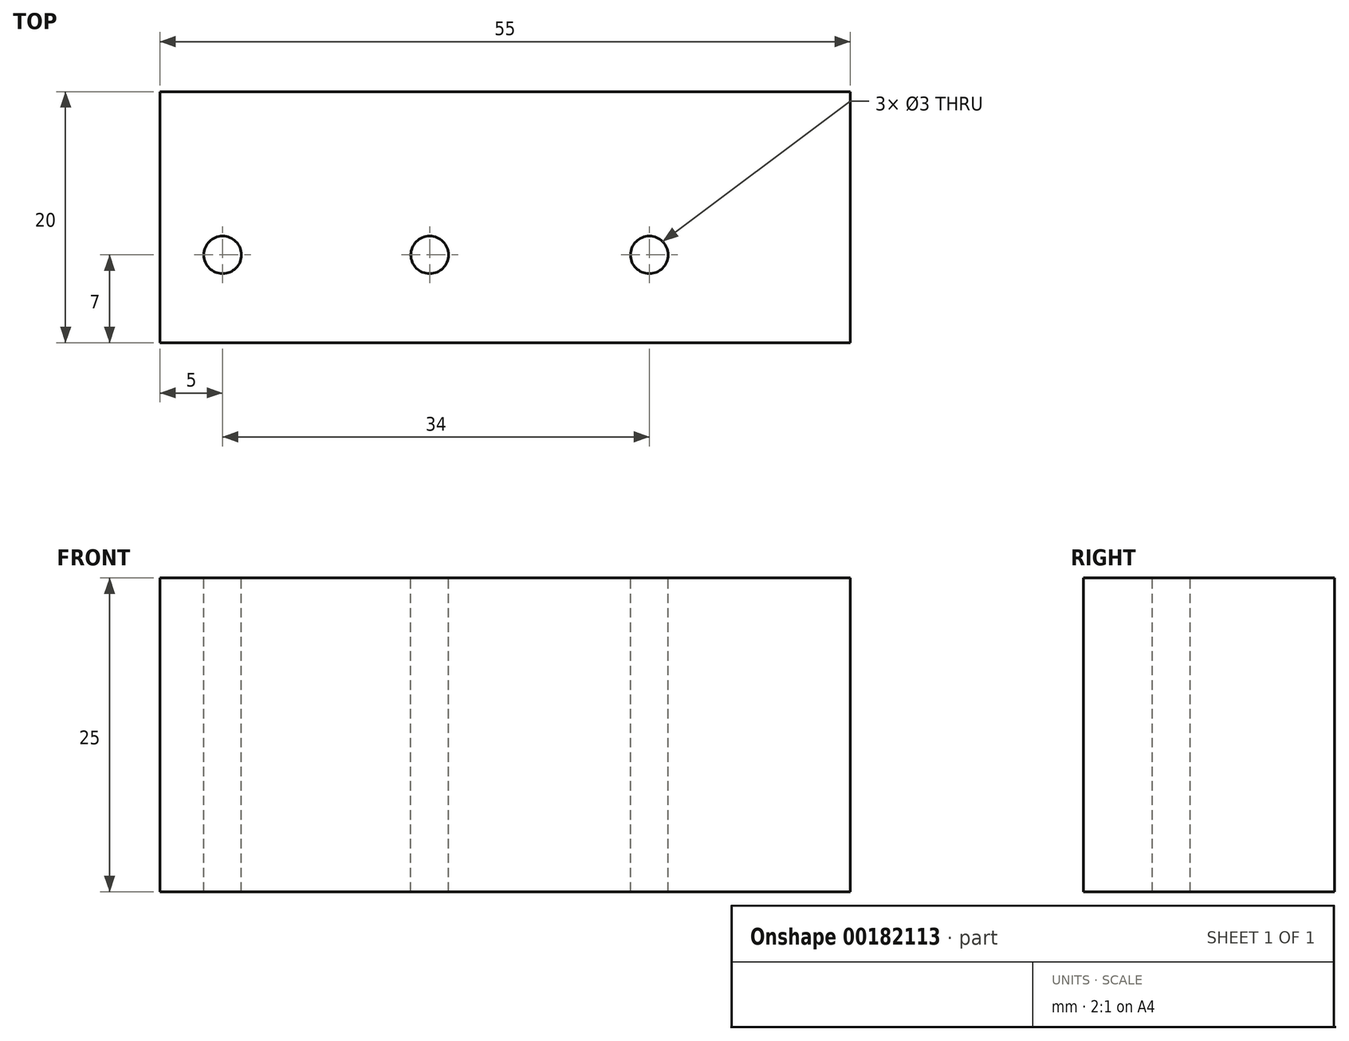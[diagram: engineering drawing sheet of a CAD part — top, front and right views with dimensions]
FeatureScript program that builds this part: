
annotation { "Feature Type Name" : "Feature", "Feature Type Description" : "" }
export const myFeature = defineFeature(function(context is Context, id is Id, definition is map)
    precondition{}
    {
        {
            var Q0;
            Q0=qCreatedBy(makeId("Top.planeOp"),FACE);
            var sketch = newSketch(context, id + "F0", { "sketchPlane" : qUnion([Q0])});
            skLineSegment(sketch, "E0.bottom", {"start": v(-27.5, 10) * mm, "end": v(27.5, 10) * mm});
            skLineSegment(sketch, "E0.top", {"start": v(-27.5, -10) * mm, "end": v(27.5, -10) * mm});
            skLineSegment(sketch, "E0.left", {"start": v(-27.5, 10) * mm, "end": v(-27.5, -10) * mm});
            skLineSegment(sketch, "E0.right", {"start": v(27.5, 10) * mm, "end": v(27.5, -10) * mm});
            skSolve(sketch);
        }
        {
            var Q0;
            Q0=qSketchRegion(id+"F0",true);
            extrude(context, id + "F1", {"entities" : qUnion([Q0]), "depth" : 25 * mm});
        }
        {
            var Q0;
            Q0=makeQuery(id+"F1.opExtrude","CAP_FACE",FACE,{"disambiguationData":[OSD([sQuery(id+"F0.wireOp",EDGE,"E0.bottom"),sQuery(id+"F0.wireOp",EDGE,"E0.top"),sQuery(id+"F0.wireOp",EDGE,"E0.left"),sQuery(id+"F0.wireOp",EDGE,"E0.right")])],"isStart":false});
            var sketch = newSketch(context, id + "F2", { "sketchPlane" : qUnion([Q0])});
            skCircle(sketch, "E1", {"center": v(-22.5, -3) * mm, "radius": 1.5 * mm});
            skSolve(sketch);
        }
        {
            var Q0;
            Q0=qSketchRegion(id+"F2",true);
            extrude(context, id + "F3", {"entities" : qUnion([Q0]), "operationType" : NewBodyOperationType.REMOVE, "endBound" : BoundingType.THROUGH_ALL, "oppositeDirection" : true, "depth" : 25 * mm});
        }
        {
            var Q0;
            Q0=makeQuery(id+"F1.opExtrude","CAP_FACE",FACE,{"disambiguationData":[OSD([sQuery(id+"F0.wireOp",EDGE,"E0.bottom"),sQuery(id+"F0.wireOp",EDGE,"E0.top"),sQuery(id+"F0.wireOp",EDGE,"E0.left"),sQuery(id+"F0.wireOp",EDGE,"E0.right")])],"isStart":false});
            var sketch = newSketch(context, id + "F4", { "sketchPlane" : qUnion([Q0])});
            skCircle(sketch, "E2", {"center": v(-6, -3) * mm, "radius": 1.5 * mm});
            skSolve(sketch);
        }
        {
            var Q0;
            Q0=qSketchRegion(id+"F4",true);
            extrude(context, id + "F5", {"entities" : qUnion([Q0]), "operationType" : NewBodyOperationType.REMOVE, "endBound" : BoundingType.THROUGH_ALL, "oppositeDirection" : true, "depth" : 25 * mm});
        }
        {
            var Q0;
            Q0=makeQuery(id+"F1.opExtrude","CAP_FACE",FACE,{"disambiguationData":[OSD([sQuery(id+"F0.wireOp",EDGE,"E0.bottom"),sQuery(id+"F0.wireOp",EDGE,"E0.top"),sQuery(id+"F0.wireOp",EDGE,"E0.left"),sQuery(id+"F0.wireOp",EDGE,"E0.right")])],"isStart":false});
            var sketch = newSketch(context, id + "F6", { "sketchPlane" : qUnion([Q0])});
            skCircle(sketch, "E3", {"center": v(11.5, -3) * mm, "radius": 1.5 * mm});
            skSolve(sketch);
        }
        {
            var Q0;
            Q0=qSketchRegion(id+"F6",true);
            extrude(context, id + "F7", {"entities" : qUnion([Q0]), "operationType" : NewBodyOperationType.REMOVE, "endBound" : BoundingType.THROUGH_ALL, "oppositeDirection" : true, "depth" : 25 * mm});
        }
    });
